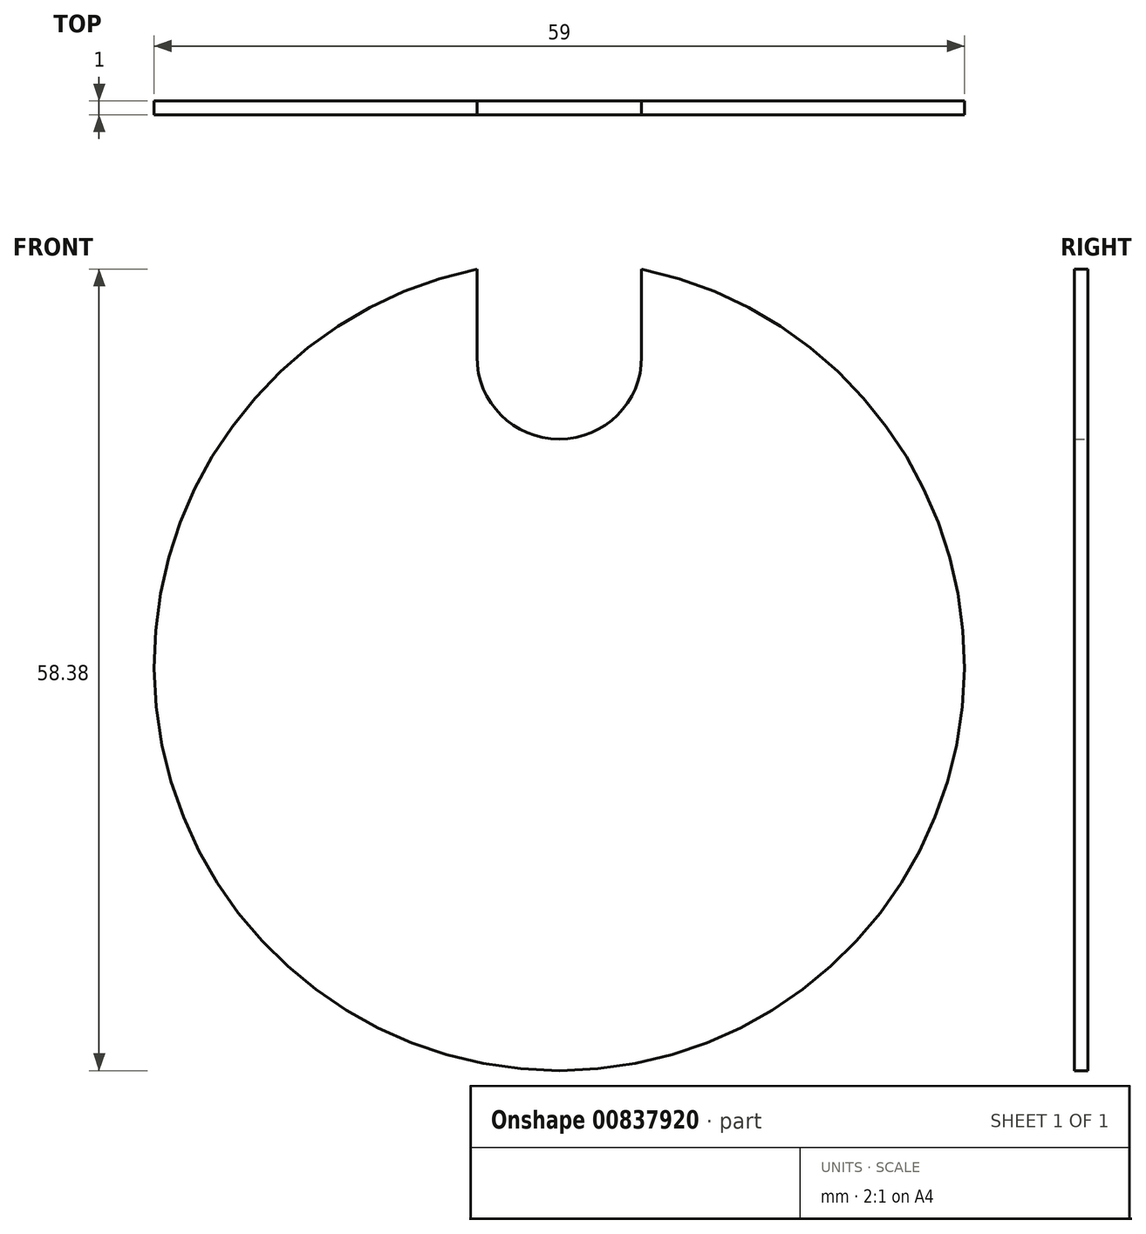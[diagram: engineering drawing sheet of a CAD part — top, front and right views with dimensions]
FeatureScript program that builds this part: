
annotation { "Feature Type Name" : "Feature", "Feature Type Description" : "" }
export const myFeature = defineFeature(function(context is Context, id is Id, definition is map)
    precondition{}
    {
        {
            var Q0;
            Q0=qCreatedBy(makeId("Front.planeOp"),FACE);
            var sketch = newSketch(context, id + "F0", { "sketchPlane" : qUnion([Q0])});
            skCircle(sketch, "E0", {"center": v(0, 0) * mm, "radius": 29.5 * mm});
            skLineSegment(sketch, "E1", {"start": v(0, 29.5) * mm, "end": v(0, 22.5) * mm});
            skCircle(sketch, "E2", {"center": v(0, 22.5) * mm, "radius": 6 * mm});
            skLineSegment(sketch, "E3.bottom", {"start": v(-6, 22.5) * mm, "end": v(6, 22.5) * mm});
            skLineSegment(sketch, "E3.top", {"start": v(-6, 29.57) * mm, "end": v(6, 29.57) * mm});
            skLineSegment(sketch, "E3.left", {"start": v(-6, 22.5) * mm, "end": v(-6, 29.57) * mm});
            skLineSegment(sketch, "E3.right", {"start": v(6, 22.5) * mm, "end": v(6, 29.57) * mm});
            skSolve(sketch);
        }
        {
            var Q0;
            {var subQ3=sQuery(id+"F0.wireOp",EDGE,"E3.right");var subQ8=sQuery(id+"F0.wireOp",EDGE,"E0");var subQ9=makeQuery(id+"F0.imprint","INTERSECT",VERTEX,{"derivedFrom":[subQ8,subQ3]});Q0=makeQuery(id+"F0.imprint","IMPRINT",FACE,{"disambiguationData":[TD([[makeQuery(id+"F0.imprint","IMPRINT",EDGE,{"disambiguationData":[TD([[subQ9,1.0]])],"derivedFrom":subQ8}),1.0]])]});}
            extrude(context, id + "F1", {"entities" : qUnion([Q0]), "depth" : 1 * mm, "offsetDistance" : 25 * mm});
        }
    });
